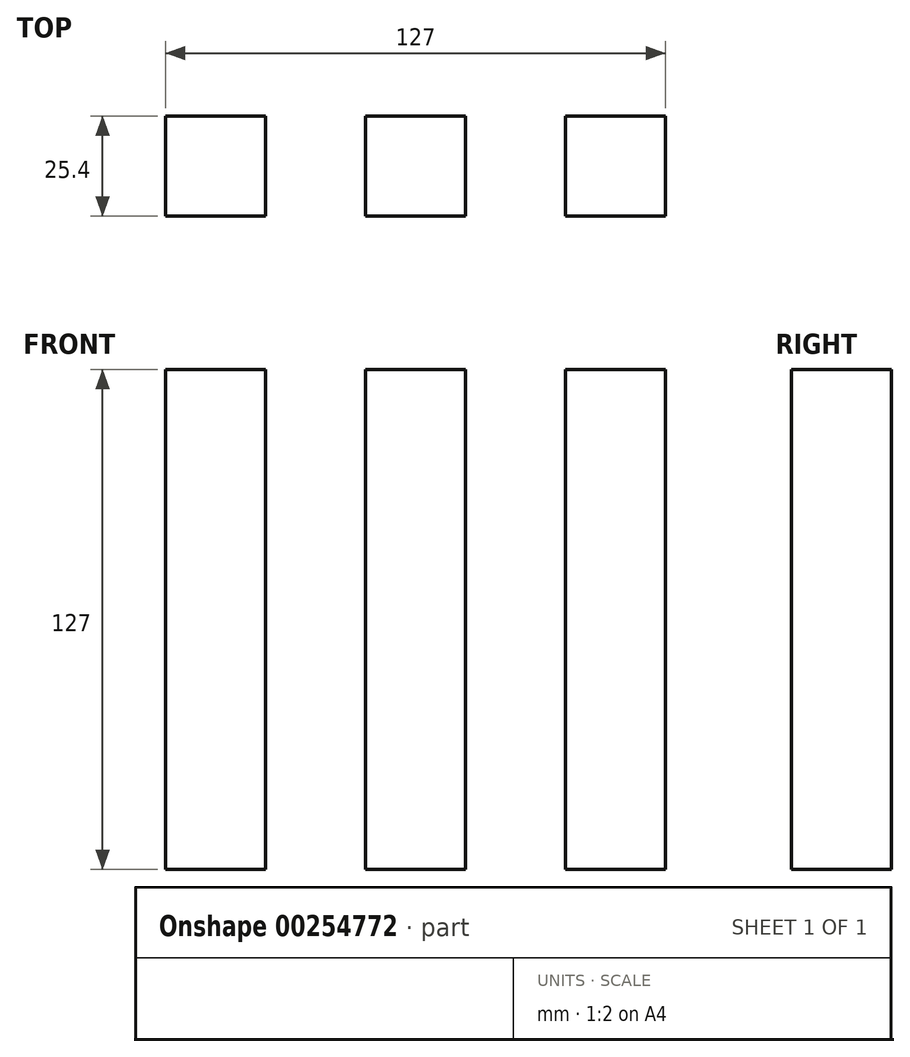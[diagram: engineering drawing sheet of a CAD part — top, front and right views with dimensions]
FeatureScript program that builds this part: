
annotation { "Feature Type Name" : "Feature", "Feature Type Description" : "" }
export const myFeature = defineFeature(function(context is Context, id is Id, definition is map)
    precondition{}
    {
        {
            var Q0;
            Q0=qCreatedBy(makeId("Top.planeOp"),FACE);
            var sketch = newSketch(context, id + "F0", { "sketchPlane" : qUnion([Q0])});
            skLineSegment(sketch, "E0.bottom", {"start": v(-12.7, -12.7) * mm, "end": v(12.7, -12.7) * mm});
            skLineSegment(sketch, "E0.top", {"start": v(-12.7, 12.7) * mm, "end": v(12.7, 12.7) * mm});
            skLineSegment(sketch, "E0.left", {"start": v(-12.7, -12.7) * mm, "end": v(-12.7, 12.7) * mm});
            skLineSegment(sketch, "E0.right", {"start": v(12.7, -12.7) * mm, "end": v(12.7, 12.7) * mm});
            skPoint(sketch, "E0.middle", {"position": v(0, 0) * mm});
            skLineSegment(sketch, "E1.bottom", {"start": v(-63.5, -12.7) * mm, "end": v(-38.1, -12.7) * mm});
            skLineSegment(sketch, "E1.top", {"start": v(-63.5, 12.7) * mm, "end": v(-38.1, 12.7) * mm});
            skLineSegment(sketch, "E1.left", {"start": v(-63.5, -12.7) * mm, "end": v(-63.5, 12.7) * mm});
            skLineSegment(sketch, "E1.right", {"start": v(-38.1, -12.7) * mm, "end": v(-38.1, 12.7) * mm});
            skPoint(sketch, "E1.middle", {"position": v(-50.8, 0) * mm});
            skLineSegment(sketch, "E2.bottom", {"start": v(63.5, -12.7) * mm, "end": v(38.1, -12.7) * mm});
            skLineSegment(sketch, "E2.top", {"start": v(63.5, 12.7) * mm, "end": v(38.1, 12.7) * mm});
            skLineSegment(sketch, "E2.left", {"start": v(63.5, -12.7) * mm, "end": v(63.5, 12.7) * mm});
            skLineSegment(sketch, "E2.right", {"start": v(38.1, -12.7) * mm, "end": v(38.1, 12.7) * mm});
            skPoint(sketch, "E2.middle", {"position": v(50.8, 0) * mm});
            skSolve(sketch);
        }
        {
            var Q0;
            Q0=makeQuery(id+"F0.imprint","IMPRINT",FACE,{"disambiguationData":[TD([[makeQuery(id+"F0.imprint","IMPRINT",EDGE,{"derivedFrom":sQuery(id+"F0.wireOp",EDGE,"E1.bottom")}),1.0]])]});
            var Q1;
            Q1=makeQuery(id+"F0.imprint","IMPRINT",FACE,{"disambiguationData":[TD([[makeQuery(id+"F0.imprint","IMPRINT",EDGE,{"derivedFrom":sQuery(id+"F0.wireOp",EDGE,"E0.bottom")}),1.0]])]});
            var Q2;
            Q2=makeQuery(id+"F0.imprint","IMPRINT",FACE,{"disambiguationData":[TD([[makeQuery(id+"F0.imprint","IMPRINT",EDGE,{"derivedFrom":sQuery(id+"F0.wireOp",EDGE,"E2.bottom")}),-1.0]])]});
            extrude(context, id + "F1", {"entities" : qUnion([Q0, Q1, Q2]), "endBound" : BoundingType.SYMMETRIC, "depth" : 127 * mm});
        }
    });
